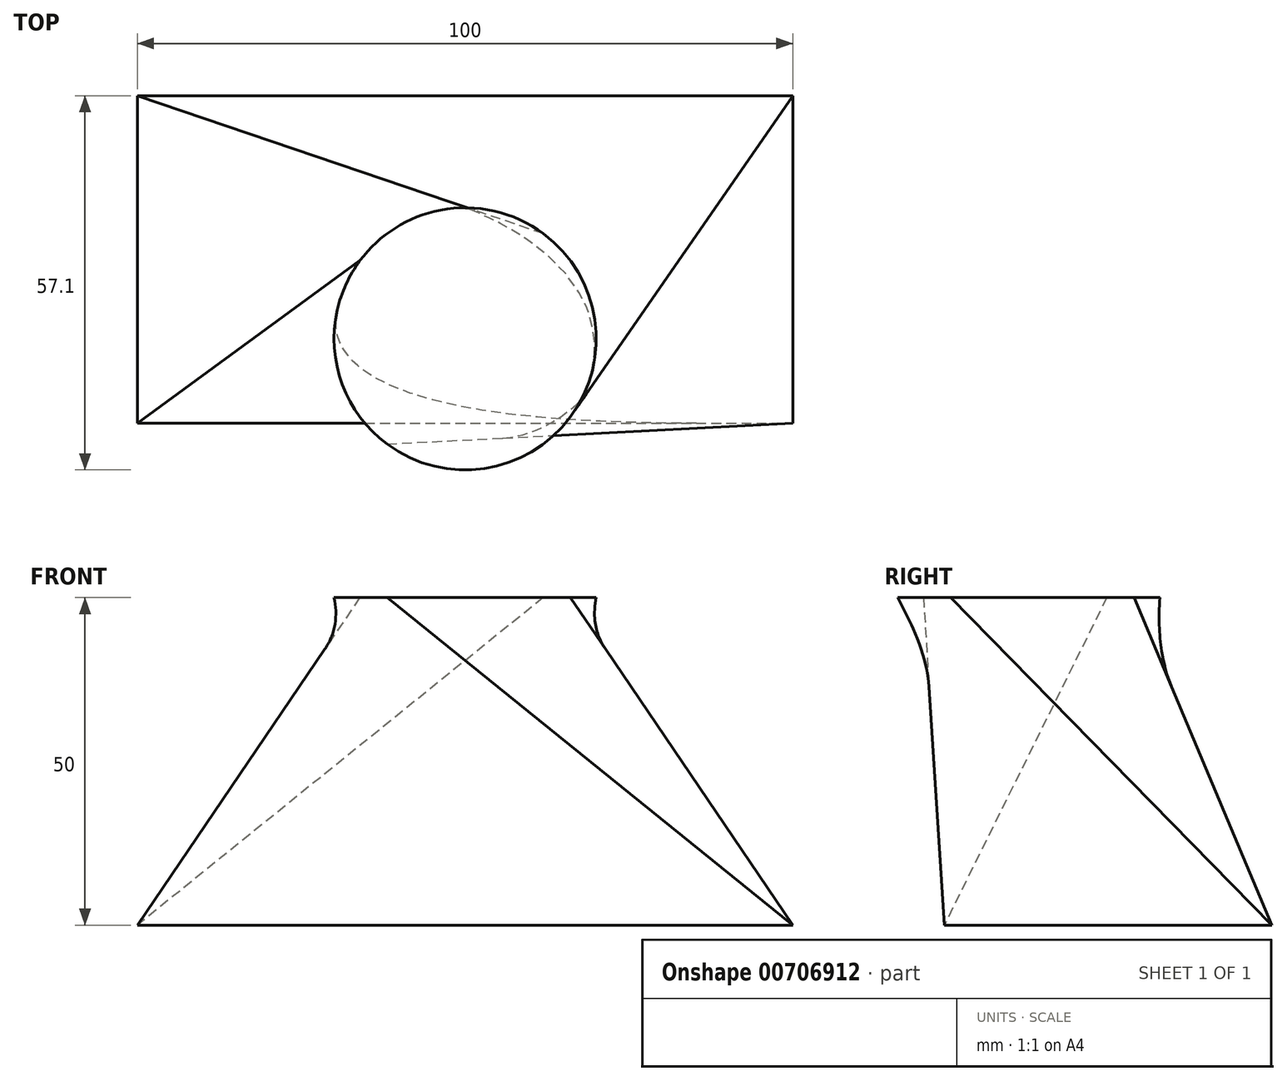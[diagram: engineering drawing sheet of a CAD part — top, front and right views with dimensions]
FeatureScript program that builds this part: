
annotation { "Feature Type Name" : "Feature", "Feature Type Description" : "" }
export const myFeature = defineFeature(function(context is Context, id is Id, definition is map)
    precondition{}
    {
        {
            var Q0;
            Q0=qCreatedBy(makeId("Top.planeOp"),FACE);
            var sketch = newSketch(context, id + "F0", { "sketchPlane" : qUnion([Q0])});
            skLineSegment(sketch, "E0.bottom", {"start": v(-50, 0) * mm, "end": v(50, 0) * mm});
            skLineSegment(sketch, "E0.top", {"start": v(-50, -50) * mm, "end": v(50, -50) * mm});
            skLineSegment(sketch, "E0.left", {"start": v(-50, 0) * mm, "end": v(-50, -50) * mm});
            skLineSegment(sketch, "E0.right", {"start": v(50, 0) * mm, "end": v(50, -50) * mm});
            skSolve(sketch);
        }
        {
            var Q0;
            Q0=qCreatedBy(makeId("Top.planeOp"),FACE);
            cPlane(context, id + "F1", {"entities" : qUnion([Q0]), "cplaneType" : CPlaneType.OFFSET, "offset" : 50 * mm, "width" : 150 * mm, "height" : 150 * mm});
        }
        {
            var Q0;
            Q0=qCreatedBy(id+"F1.planeOp",FACE);
            var sketch = newSketch(context, id + "F2", { "sketchPlane" : qUnion([Q0])});
            skCircle(sketch, "E1", {"center": v(0, -37.1) * mm, "radius": 20 * mm});
            skSolve(sketch);
        }
        {
            var Q0;
            Q0=makeQuery(id+"F2.imprint","IMPRINT",FACE,{"disambiguationData":[TD([[makeQuery(id+"F2.imprint","IMPRINT",EDGE,{"derivedFrom":sQuery(id+"F2.wireOp",EDGE,"E1")}),1.0]])]});
            var Q1;
            Q1=makeQuery(id+"F0.imprint","IMPRINT",FACE,{"disambiguationData":[TD([[makeQuery(id+"F0.imprint","IMPRINT",EDGE,{"derivedFrom":sQuery(id+"F0.wireOp",EDGE,"E0.bottom")}),-1.0]])]});
            loft(context, id + "F3", {"sheetProfilesArray" : [{ "sheetProfileEntities" : qUnion([Q0]) }, { "sheetProfileEntities" : qUnion([Q1]) }]});
        }
    });
